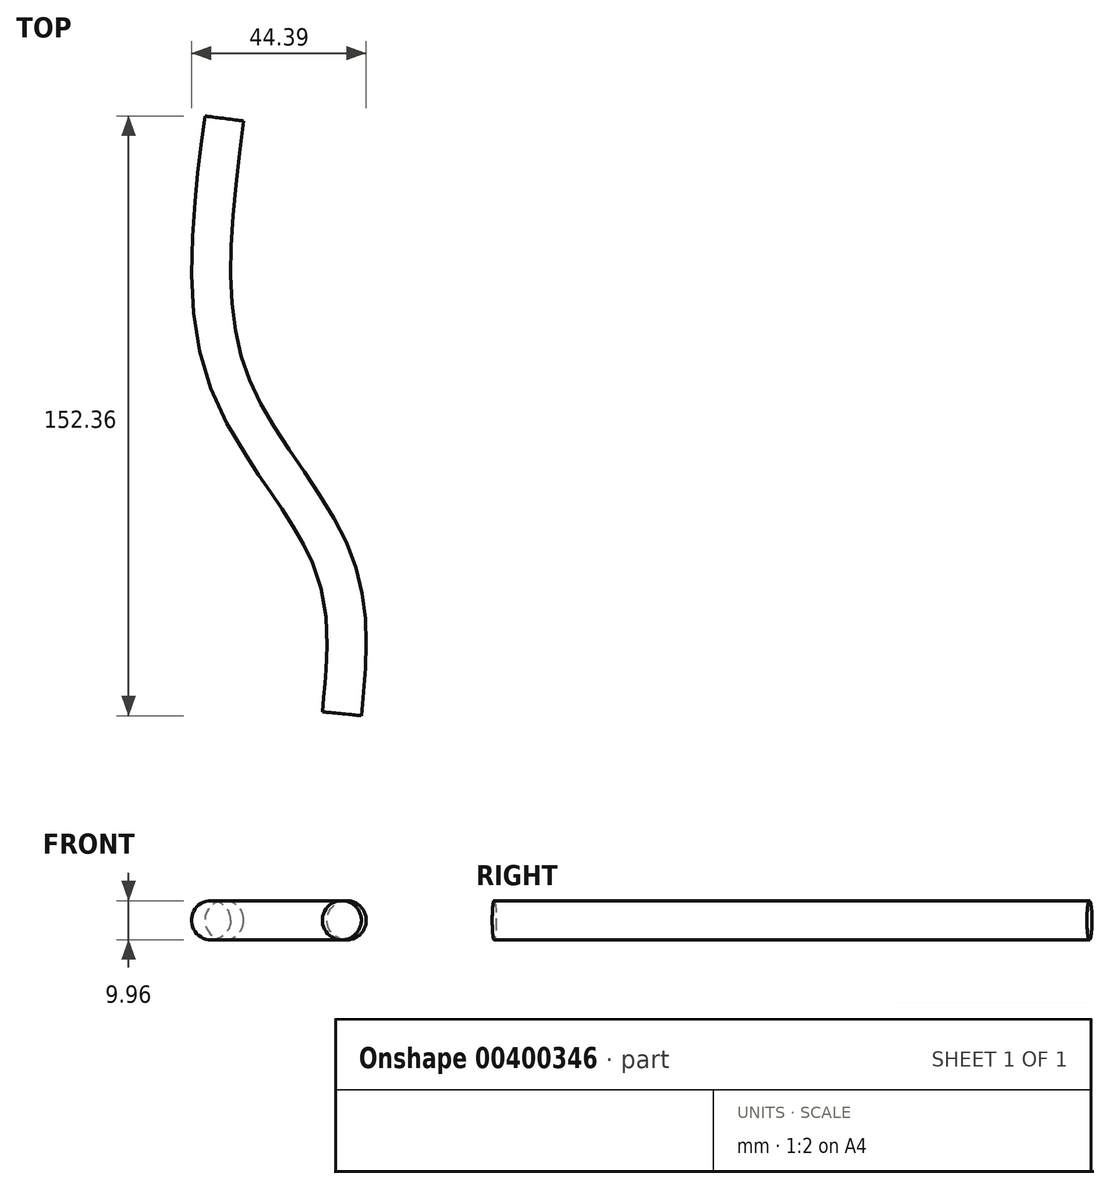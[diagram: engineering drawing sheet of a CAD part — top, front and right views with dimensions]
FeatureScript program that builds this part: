
annotation { "Feature Type Name" : "Feature", "Feature Type Description" : "" }
export const myFeature = defineFeature(function(context is Context, id is Id, definition is map)
    precondition{}
    {
        {
            var Q0;
            Q0=qCreatedBy(makeId("Top.planeOp"),FACE);
            var sketch = newSketch(context, id + "F0", { "sketchPlane" : qUnion([Q0])});
            skFitSpline(sketch, "E0", {"points": [v(-23.4, 75.32) * mm, v(-22.42, 8.91) * mm, v(4.14, -37.09) * mm, v(6.47, -75.93) * mm], "startDerivative": vector(-24.32, -187.71) * mm, "endDerivative": vector(-13.8, -136.82) * mm});
            skSolve(sketch);
        }
        {
            var Q0;
            Q0=sQuery(id+"F0.wireOp",EDGE,"E0");
            var Q1;
            Q1=sQuery(id+"F0.wireOp",VERTEX,"E0.3.internal");
            cPlane(context, id + "F1", {"entities" : qUnion([Q0, Q1]), "cplaneType" : CPlaneType.CURVE_POINT, "offset" : 25.4 * mm, "width" : 152.4 * mm, "height" : 152.4 * mm});
        }
        {
            var Q0;
            Q0=qCreatedBy(id+"F1.planeOp",FACE);
            var sketch = newSketch(context, id + "F2", { "sketchPlane" : qUnion([Q0])});
            skCircle(sketch, "E1", {"center": v(14.8, 0) * mm, "radius": 4.98 * mm});
            skSolve(sketch);
        }
        {
            var Q0;
            Q0=makeQuery(id+"F2.imprint","IMPRINT",FACE,{"disambiguationData":[TD([[makeQuery(id+"F2.imprint","IMPRINT",EDGE,{"derivedFrom":sQuery(id+"F2.wireOp",EDGE,"E1")}),1.0]])]});
            var Q1;
            Q1=sQuery(id+"F0.wireOp",EDGE,"E0");
            sweep(context, id + "F3", {"profiles" : qUnion([Q0]), "path" : qUnion([Q1])});
        }
    });
